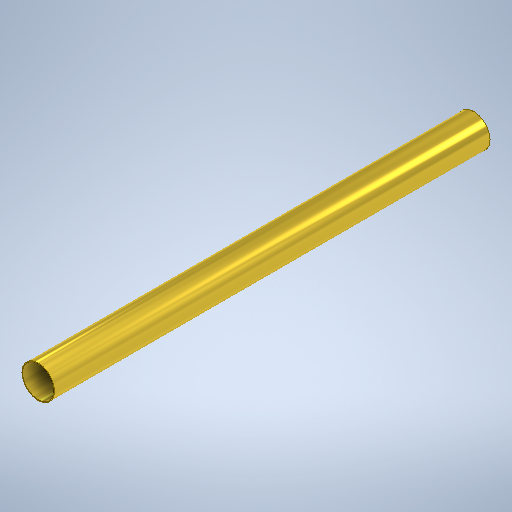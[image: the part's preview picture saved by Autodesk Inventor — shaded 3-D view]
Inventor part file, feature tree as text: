
AUTODESK INVENTOR PART (.ipt)
format: ipt  version: 2025.2 (Build 292293000, 293)  size: 249,856 bytes
history: native  units: mm
features: other x1, extrude x1, sketch x1
ambient origin geometry x8: Origin, YZ Plane, XZ Plane, XY Plane, X Axis, Y Axis, Z Axis, Center Point
bodies: Body1 (feature_tree)
feature tree (3):
  other  "Sólido1"
  extrude  "Extrusão1"  Depth=2000.0mm
  sketch  "Esboço1"  dims[d0=150.0mm d1=3.0mm d2=2000.0mm d3=0.0mm d4=0.5mm d5=0.872665mm]
